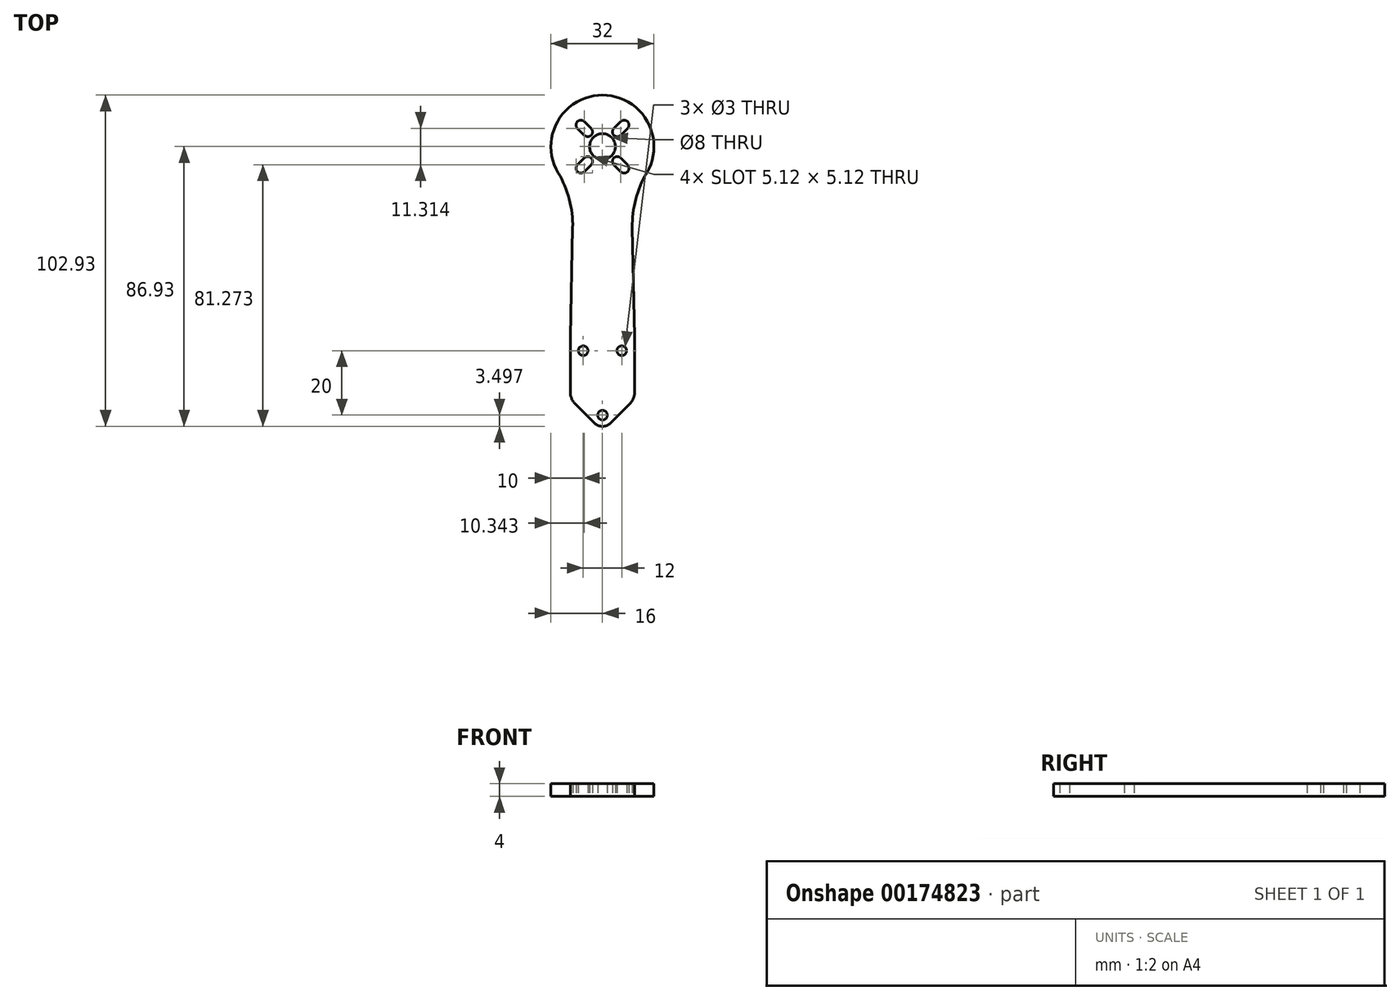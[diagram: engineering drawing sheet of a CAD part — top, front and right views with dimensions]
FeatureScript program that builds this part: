
annotation { "Feature Type Name" : "Feature", "Feature Type Description" : "" }
export const myFeature = defineFeature(function(context is Context, id is Id, definition is map)
    precondition{}
    {
        {
            var Q0;
            Q0=qCreatedBy(makeId("Top.planeOp"),FACE);
            var sketch = newSketch(context, id + "F0", { "sketchPlane" : qUnion([Q0])});
            skCircle(sketch, "E0", {"center": v(0, 0) * mm, "radius": 105 * mm, "construction": true});
            skLineSegment(sketch, "E1", {"start": v(0, 0) * mm, "end": v(0, 105) * mm, "construction": true});
            skCircle(sketch, "E2", {"center": v(0, 21.57) * mm, "radius": 1.5 * mm});
            skLineSegment(sketch, "E3", {"start": v(-6, 41.57) * mm, "end": v(6, 41.57) * mm, "construction": true});
            skCircle(sketch, "E4", {"center": v(-6, 41.57) * mm, "radius": 1.5 * mm});
            skCircle(sketch, "E5", {"center": v(6, 41.57) * mm, "radius": 1.5 * mm});
            skCircle(sketch, "E6", {"center": v(0, 105) * mm, "radius": 4 * mm});
            skLineSegment(sketch, "E7.left", {"start": v(-10, 46) * mm, "end": v(-10, 26.62) * mm});
            skLineSegment(sketch, "E7.right", {"start": v(10, 46) * mm, "end": v(10, 26.62) * mm});
            skLineSegment(sketch, "E8", {"start": v(-9, 91.77) * mm, "end": v(-10, 46) * mm});
            skLineSegment(sketch, "E9", {"start": v(9, 91.77) * mm, "end": v(10, 46) * mm});
            skLineSegment(sketch, "E10", {"start": v(0, 21.57) * mm, "end": v(-21.57, 0) * mm, "construction": true});
            skLineSegment(sketch, "E11", {"start": v(-21.57, 0) * mm, "end": v(0, -21.57) * mm, "construction": true});
            skLineSegment(sketch, "E12", {"start": v(0, -21.57) * mm, "end": v(21.57, 0) * mm, "construction": true});
            skLineSegment(sketch, "E13", {"start": v(21.57, 0) * mm, "end": v(0, 21.57) * mm, "construction": true});
            skLineSegment(sketch, "E14", {"start": v(-11.31, 93.69) * mm, "end": v(11.31, 116.31) * mm, "construction": true});
            skLineSegment(sketch, "E15", {"start": v(-11.31, 116.31) * mm, "end": v(11.31, 93.69) * mm, "construction": true});
            skArc(sketch, "E16", {"start": v(3.54, 110.66) * mm, "mid": v(3.54, 108.54) * mm, "end": v(5.66, 108.54) * mm});
            skArc(sketch, "E17", {"start": v(7.78, 110.66) * mm, "mid": v(7.78, 112.78) * mm, "end": v(5.66, 112.78) * mm});
            skLineSegment(sketch, "E18", {"start": v(5.66, 108.54) * mm, "end": v(7.78, 110.66) * mm});
            skLineSegment(sketch, "E19", {"start": v(5.66, 112.78) * mm, "end": v(3.54, 110.66) * mm});
            skArc(sketch, "E20.1.0", {"start": v(-5.66, 108.54) * mm, "mid": v(-3.54, 108.54) * mm, "end": v(-3.54, 110.66) * mm});
            skArc(sketch, "E20.1.1", {"start": v(-5.66, 112.78) * mm, "mid": v(-7.78, 112.78) * mm, "end": v(-7.78, 110.66) * mm});
            skLineSegment(sketch, "E20.1.2", {"start": v(-7.78, 110.66) * mm, "end": v(-5.66, 108.54) * mm});
            skLineSegment(sketch, "E20.1.3", {"start": v(-3.54, 110.66) * mm, "end": v(-5.66, 112.78) * mm});
            skArc(sketch, "E20.2.0", {"start": v(-3.54, 99.34) * mm, "mid": v(-3.54, 101.46) * mm, "end": v(-5.66, 101.46) * mm});
            skArc(sketch, "E20.2.1", {"start": v(-7.78, 99.34) * mm, "mid": v(-7.78, 97.22) * mm, "end": v(-5.66, 97.22) * mm});
            skLineSegment(sketch, "E20.2.2", {"start": v(-5.66, 97.22) * mm, "end": v(-3.54, 99.34) * mm});
            skLineSegment(sketch, "E20.2.3", {"start": v(-5.66, 101.46) * mm, "end": v(-7.78, 99.34) * mm});
            skArc(sketch, "E20.3.0", {"start": v(5.66, 101.46) * mm, "mid": v(3.54, 101.46) * mm, "end": v(3.54, 99.34) * mm});
            skArc(sketch, "E20.3.1", {"start": v(5.66, 97.22) * mm, "mid": v(7.78, 97.22) * mm, "end": v(7.78, 99.34) * mm});
            skLineSegment(sketch, "E20.3.2", {"start": v(7.78, 99.34) * mm, "end": v(5.66, 101.46) * mm});
            skLineSegment(sketch, "E20.3.3", {"start": v(3.54, 99.34) * mm, "end": v(5.66, 97.22) * mm});
            skArc(sketch, "E21.cCircle", {"start": v(9, 91.77) * mm, "mid": v(0, 121) * mm, "end": v(-9, 91.77) * mm});
            skArc(sketch, "E22", {"start": v(-2.47, 19.1) * mm, "mid": v(0, 18.07) * mm, "end": v(2.47, 19.1) * mm});
            skLineSegment(sketch, "E23", {"start": v(-10, 26.62) * mm, "end": v(-2.47, 19.1) * mm});
            skLineSegment(sketch, "E24", {"start": v(10, 26.62) * mm, "end": v(2.47, 19.1) * mm});
            skSolve(sketch);
        }
        {
            var Q0;
            Q0 = qSketchRegion(id + "F0", true);
            extrude(context, id + "F1", {"entities" : qUnion([Q0]), "depth" : 4 * mm});
        }
        {
            var Q0;
            Q0=makeQuery(id+"F1.opExtrude","SWEPT_EDGE",EDGE,{"disambiguationData":[OSD([sQuery(id+"F0.wireOp",EDGE,"E21.4"),sQuery(id+"F0.wireOp",EDGE,"E21.5")])]});
            var Q1;
            Q1=makeQuery(id+"F1.opExtrude","SWEPT_EDGE",EDGE,{"disambiguationData":[OSD([sQuery(id+"F0.wireOp",EDGE,"E21.5"),sQuery(id+"F0.wireOp",EDGE,"E21.6")])]});
            var Q2;
            Q2=makeQuery(id+"F1.opExtrude","SWEPT_EDGE",EDGE,{"disambiguationData":[OSD([sQuery(id+"F0.wireOp",EDGE,"E21.6"),sQuery(id+"F0.wireOp",EDGE,"E21.7")])]});
            var Q3;
            Q3=makeQuery(id+"F1.opExtrude","SWEPT_EDGE",EDGE,{"disambiguationData":[OSD([sQuery(id+"F0.wireOp",EDGE,"E21.0"),sQuery(id+"F0.wireOp",EDGE,"E21.7")])]});
            var Q4;
            Q4=makeQuery(id+"F1.opExtrude","SWEPT_EDGE",EDGE,{"disambiguationData":[OSD([sQuery(id+"F0.wireOp",EDGE,"E21.0"),sQuery(id+"F0.wireOp",EDGE,"E21.1")])]});
            var Q5;
            Q5=makeQuery(id+"F1.opExtrude","SWEPT_EDGE",EDGE,{"disambiguationData":[OSD([sQuery(id+"F0.wireOp",EDGE,"E21.1"),sQuery(id+"F0.wireOp",EDGE,"E21.2")])]});
            var Q6;
            Q6=makeQuery(id+"F1.opExtrude","SWEPT_EDGE",EDGE,{"disambiguationData":[OSD([sQuery(id+"F0.wireOp",EDGE,"E7.right"),sQuery(id+"F0.wireOp",EDGE,"E9")])]});
            var Q7;
            Q7=makeQuery(id+"F1.opExtrude","SWEPT_EDGE",EDGE,{"disambiguationData":[OSD([sQuery(id+"F0.wireOp",EDGE,"E7.left"),sQuery(id+"F0.wireOp",EDGE,"E8")])]});
            var Q8;
            Q8=makeQuery(id+"F1.opExtrude","SWEPT_EDGE",EDGE,{"disambiguationData":[OSD([sQuery(id+"F0.wireOp",EDGE,"E7.left"),sQuery(id+"F0.wireOp",EDGE,"E23")])]});
            var Q9;
            Q9=makeQuery(id+"F1.opExtrude","SWEPT_EDGE",EDGE,{"disambiguationData":[OSD([sQuery(id+"F0.wireOp",EDGE,"E7.right"),sQuery(id+"F0.wireOp",EDGE,"E24")])]});
            fillet(context, id + "F2", {"entities" : qUnion([Q0, Q1, Q2, Q3, Q4, Q5, Q6, Q7, Q8, Q9]), "radius" : 5 * mm, "tangentPropagation" : true, "allowEdgeOverflow" : false});
        }
        {
            var Q0;
            Q0=makeQuery(id+"F1.opExtrude","SWEPT_EDGE",EDGE,{"disambiguationData":[OSD([sQuery(id+"F0.wireOp",EDGE,"E8"),sQuery(id+"F0.wireOp",EDGE,"E21.4")])]});
            var Q1;
            Q1=makeQuery(id+"F1.opExtrude","SWEPT_EDGE",EDGE,{"disambiguationData":[OSD([sQuery(id+"F0.wireOp",EDGE,"E9"),sQuery(id+"F0.wireOp",EDGE,"E21.2")])]});
            fillet(context, id + "F3", {"entities" : qUnion([Q0, Q1]), "radius" : 32 * mm, "tangentPropagation" : true, "allowEdgeOverflow" : false});
        }
    });
